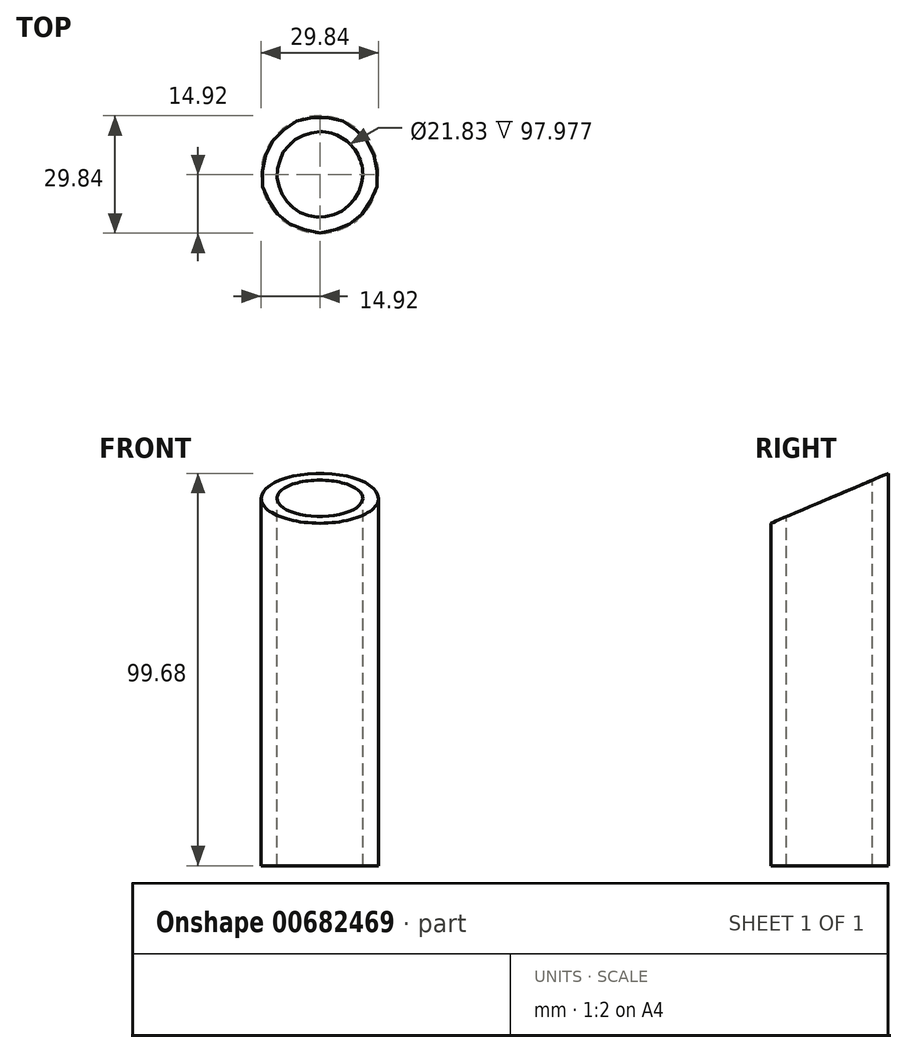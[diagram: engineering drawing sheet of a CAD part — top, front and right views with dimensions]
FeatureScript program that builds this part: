
annotation { "Feature Type Name" : "Feature", "Feature Type Description" : "" }
export const myFeature = defineFeature(function(context is Context, id is Id, definition is map)
    precondition{}
    {
        {
            var Q0;
            Q0=qCreatedBy(makeId("Top.planeOp"),FACE);
            var sketch = newSketch(context, id + "F0", { "sketchPlane" : qUnion([Q0])});
            skCircle(sketch, "E0", {"center": v(0, 0) * mm, "radius": 14.92 * mm});
            skSolve(sketch);
        }
        {
            var Q0;
            Q0 = qSketchRegion(id + "F0", true);
            extrude(context, id + "F1", {"entities" : qUnion([Q0]), "depth" : 101.6 * mm, "offsetDistance" : 25.4 * mm});
        }
        {
            var Q0;
            Q0=makeQuery(id+"F1.opExtrude","CAP_FACE",FACE,{"disambiguationData":[OSD([sQuery(id+"F0.wireOp",EDGE,"E0")])],"isStart":false});
            var sketch = newSketch(context, id + "F2", { "sketchPlane" : qUnion([Q0])});
            skCircle(sketch, "E1", {"center": v(0, 0) * mm, "radius": 10.92 * mm});
            skSolve(sketch);
        }
        {
            var Q0;
            Q0 = qSketchRegion(id + "F2", true);
            extrude(context, id + "F3", {"entities" : qUnion([Q0]), "operationType" : NewBodyOperationType.REMOVE, "oppositeDirection" : true, "depth" : 127 * mm, "offsetDistance" : 25.4 * mm});
        }
        {
            var Q0;
            Q0=qCreatedBy(makeId("Right.planeOp"),FACE);
            var sketch = newSketch(context, id + "F4", { "sketchPlane" : qUnion([Q0])});
            skLineSegment(sketch, "E2", {"start": v(20.34, 101.98) * mm, "end": v(-28.05, 81.42) * mm});
            skLineSegment(sketch, "E3", {"start": v(-28.05, 81.42) * mm, "end": v(-28.05, 105.4) * mm});
            skLineSegment(sketch, "E4", {"start": v(-28.05, 105.4) * mm, "end": v(20.34, 101.98) * mm});
            skLineSegment(sketch, "E5", {"start": v(-28.05, 101.98) * mm, "end": v(20.34, 101.98) * mm});
            skSolve(sketch);
        }
        {
            var Q0;
            {var subQ0=sQuery(id+"F4.wireOp",EDGE,"E2");Q0=makeQuery(id+"F4.imprint","IMPRINT",FACE,{"disambiguationData":[TD([[makeQuery(id+"F4.imprint","IMPRINT",EDGE,{"derivedFrom":subQ0}),-1.0]])]});}
            extrude(context, id + "F5", {"entities" : qUnion([Q0]), "operationType" : NewBodyOperationType.REMOVE, "oppositeDirection" : true, "depth" : 152.4 * mm, "offsetDistance" : 25.4 * mm});
        }
        {
            var Q0;
            {var subQ0=sQuery(id+"F4.wireOp",EDGE,"E2");Q0=makeQuery(id+"F4.imprint","IMPRINT",FACE,{"disambiguationData":[TD([[makeQuery(id+"F4.imprint","IMPRINT",EDGE,{"derivedFrom":subQ0}),-1.0]])]});}
            extrude(context, id + "F6", {"entities" : qUnion([Q0]), "operationType" : NewBodyOperationType.REMOVE, "oppositeDirection" : true, "depth" : 152.4 * mm, "offsetDistance" : 25.4 * mm});
        }
        {
            var Q0;
            {var subQ0=sQuery(id+"F4.wireOp",EDGE,"E2");Q0=makeQuery(id+"F4.imprint","IMPRINT",FACE,{"disambiguationData":[TD([[makeQuery(id+"F4.imprint","IMPRINT",EDGE,{"derivedFrom":subQ0}),-1.0]])]});}
            extrude(context, id + "F7", {"entities" : qUnion([Q0]), "operationType" : NewBodyOperationType.REMOVE, "depth" : 81.03 * mm, "offsetDistance" : 25.4 * mm});
        }
    });
